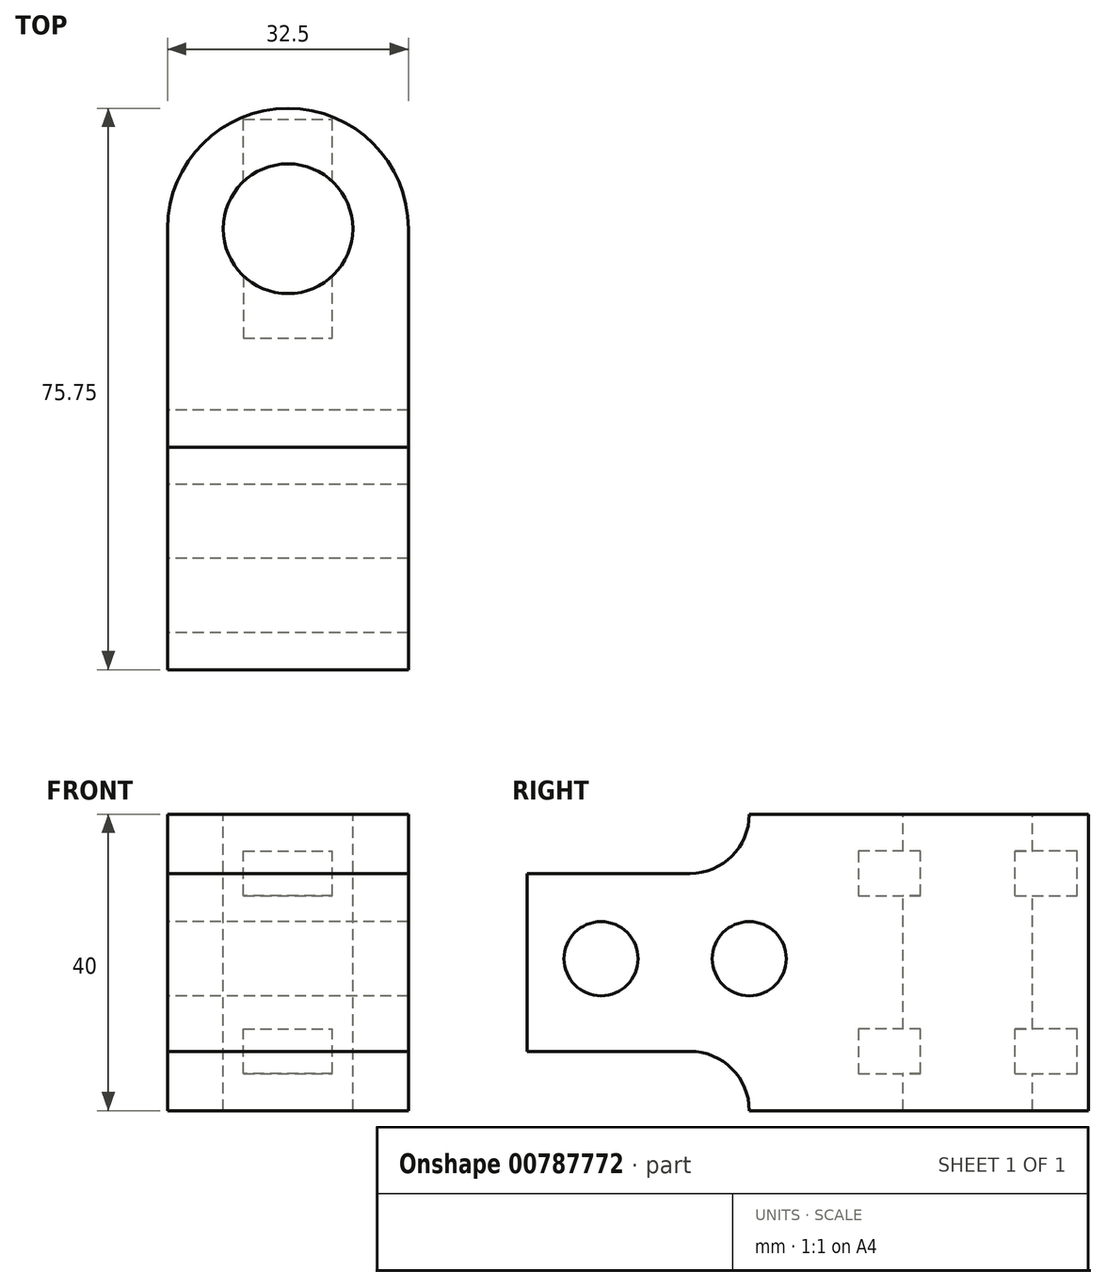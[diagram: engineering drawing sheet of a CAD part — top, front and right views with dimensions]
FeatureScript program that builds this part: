
annotation { "Feature Type Name" : "Feature", "Feature Type Description" : "" }
export const myFeature = defineFeature(function(context is Context, id is Id, definition is map)
    precondition{}
    {
        {
            var Q0;
            Q0=qCreatedBy(makeId("Top.planeOp"),FACE);
            var sketch = newSketch(context, id + "F0", { "sketchPlane" : qUnion([Q0])});
            skLineSegment(sketch, "E0", {"start": v(0, 0) * mm, "end": v(0, -16.25) * mm});
            skLineSegment(sketch, "E1", {"start": v(16.25, 0) * mm, "end": v(16.25, -29.5) * mm});
            skLineSegment(sketch, "E2", {"start": v(-16.25, 0) * mm, "end": v(-16.25, -29.5) * mm});
            skLineSegment(sketch, "E3", {"start": v(-16.25, -29.5) * mm, "end": v(16.25, -29.5) * mm});
            skArc(sketch, "E4", {"start": v(16.25, 0) * mm, "mid": v(0, 16.25) * mm, "end": v(-16.25, 0) * mm});
            skLineSegment(sketch, "E5", {"start": v(-16.25, -29.5) * mm, "end": v(-16.25, -59.5) * mm});
            skLineSegment(sketch, "E6", {"start": v(-16.25, -59.5) * mm, "end": v(16.25, -59.5) * mm});
            skLineSegment(sketch, "E7", {"start": v(16.25, -59.5) * mm, "end": v(16.25, -29.5) * mm});
            skSolve(sketch);
        }
        {
            var Q0;
            Q0=makeQuery(id+"F0.imprint","IMPRINT",FACE,{"disambiguationData":[TD([[makeQuery(id+"F0.imprint","IMPRINT",EDGE,{"derivedFrom":sQuery(id+"F0.wireOp",EDGE,"E1")}),-1.0]])]});
            var Q1;
            Q1=makeQuery(id+"F0.imprint","IMPRINT",FACE,{"disambiguationData":[TD([[makeQuery(id+"F0.imprint","IMPRINT",EDGE,{"derivedFrom":sQuery(id+"F0.wireOp",EDGE,"E3")}),-1.0]])]});
            extrude(context, id + "F1", {"entities" : qUnion([Q0, Q1]), "depth" : 40 * mm, "offsetDistance" : 25 * mm});
        }
        {
            var Q0;
            Q0=makeQuery(id+"F1.opExtrude","SWEPT_FACE",FACE,{"disambiguationData":[OSD([sQuery(id+"F0.wireOp",EDGE,"E2"),sQuery(id+"F0.wireOp",EDGE,"E5")])]});
            var sketch = newSketch(context, id + "F2", { "sketchPlane" : qUnion([Q0])});
            skLineSegment(sketch, "E8", {"start": v(59.5, 0) * mm, "end": v(59.5, 8) * mm});
            skLineSegment(sketch, "E9", {"start": v(59.5, 32) * mm, "end": v(59.5, 40) * mm});
            skLineSegment(sketch, "E10", {"start": v(59.5, 40) * mm, "end": v(29.5, 40) * mm});
            skLineSegment(sketch, "E11", {"start": v(29.5, 40) * mm, "end": v(29.5, 40) * mm});
            skLineSegment(sketch, "E12", {"start": v(37.5, 32) * mm, "end": v(59.5, 32) * mm});
            skPoint(sketch, "E13.visualSharp", {"position": v(29.5, 32) * mm});
            skArc(sketch, "E13.filletArc", {"start": v(29.5, 40) * mm, "mid": v(31.84, 34.34) * mm, "end": v(37.5, 32) * mm});
            skLineSegment(sketch, "E14", {"start": v(29.5, 0) * mm, "end": v(59.5, 0) * mm});
            skLineSegment(sketch, "E15", {"start": v(29.5, 0) * mm, "end": v(29.5, 0) * mm});
            skLineSegment(sketch, "E16", {"start": v(37.5, 8) * mm, "end": v(59.5, 8) * mm});
            skPoint(sketch, "E17.visualSharp", {"position": v(29.5, 8) * mm});
            skArc(sketch, "E17.filletArc", {"start": v(37.5, 8) * mm, "mid": v(31.84, 5.66) * mm, "end": v(29.5, 0) * mm});
            skLineSegment(sketch, "E18", {"start": v(59.5, 8) * mm, "end": v(59.5, 20.5) * mm});
            skCircle(sketch, "E19", {"center": v(29.5, 20.5) * mm, "radius": 5 * mm});
            skCircle(sketch, "E20", {"center": v(49.5, 20.5) * mm, "radius": 5 * mm});
            skSolve(sketch);
        }
        {
            var Q0;
            Q0=makeQuery(id+"F2.imprint","IMPRINT",FACE,{"disambiguationData":[TD([[makeQuery(id+"F2.imprint","IMPRINT",EDGE,{"derivedFrom":sQuery(id+"F2.wireOp",EDGE,"E9")}),-1.0]])]});
            var Q1;
            Q1=makeQuery(id+"F2.imprint","IMPRINT",FACE,{"disambiguationData":[TD([[makeQuery(id+"F2.imprint","IMPRINT",EDGE,{"derivedFrom":sQuery(id+"F2.wireOp",EDGE,"E8")}),-1.0]])]});
            var Q2;
            Q2=makeQuery(id+"F2.imprint","IMPRINT",FACE,{"disambiguationData":[TD([[makeQuery(id+"F2.imprint","IMPRINT",EDGE,{"derivedFrom":sQuery(id+"F2.wireOp",EDGE,"E19")}),1.0]])]});
            var Q3;
            Q3=makeQuery(id+"F2.imprint","IMPRINT",FACE,{"disambiguationData":[TD([[makeQuery(id+"F2.imprint","IMPRINT",EDGE,{"derivedFrom":sQuery(id+"F2.wireOp",EDGE,"E20")}),1.0]])]});
            extrude(context, id + "F3", {"entities" : qUnion([Q0, Q1, Q2, Q3]), "operationType" : NewBodyOperationType.REMOVE, "oppositeDirection" : true, "depth" : 32.5 * mm, "offsetDistance" : 25 * mm});
        }
        {
            var Q0;
            Q0=makeQuery(id+"F1.opExtrude","CAP_FACE",FACE,{"disambiguationData":[OSD([sQuery(id+"F0.wireOp",EDGE,"E1"),sQuery(id+"F0.wireOp",EDGE,"E2"),sQuery(id+"F0.wireOp",EDGE,"E4"),sQuery(id+"F0.wireOp",EDGE,"E5"),sQuery(id+"F0.wireOp",EDGE,"E6"),sQuery(id+"F0.wireOp",EDGE,"E7")])],"isStart":false});
            var sketch = newSketch(context, id + "F4", { "sketchPlane" : qUnion([Q0])});
            skCircle(sketch, "E21", {"center": v(0, 0) * mm, "radius": 8.75 * mm});
            skSolve(sketch);
        }
        {
            var Q0;
            Q0=makeQuery(id+"F4.imprint","IMPRINT",FACE,{"disambiguationData":[TD([[makeQuery(id+"F4.imprint","IMPRINT",EDGE,{"derivedFrom":sQuery(id+"F4.wireOp",EDGE,"E21")}),1.0]])]});
            extrude(context, id + "F5", {"entities" : qUnion([Q0]), "operationType" : NewBodyOperationType.REMOVE, "oppositeDirection" : true, "depth" : 40 * mm, "offsetDistance" : 25 * mm});
        }
        {
            var Q0;
            Q0=qCreatedBy(makeId("Right.planeOp"),FACE);
            var sketch = newSketch(context, id + "F6", { "sketchPlane" : qUnion([Q0])});
            skLineSegment(sketch, "E22", {"start": v(14.75, 5) * mm, "end": v(14.75, 11) * mm});
            skLineSegment(sketch, "E23", {"start": v(14.75, 29) * mm, "end": v(14.75, 35) * mm});
            skLineSegment(sketch, "E24", {"start": v(14.75, 35) * mm, "end": v(0, 35) * mm});
            skLineSegment(sketch, "E25", {"start": v(0, 35) * mm, "end": v(-14.75, 35) * mm});
            skLineSegment(sketch, "E26", {"start": v(-14.75, 35) * mm, "end": v(-14.75, 29) * mm});
            skLineSegment(sketch, "E27", {"start": v(-14.75, 29) * mm, "end": v(14.75, 29) * mm});
            skLineSegment(sketch, "E28", {"start": v(14.75, 11) * mm, "end": v(-14.75, 11) * mm});
            skLineSegment(sketch, "E29", {"start": v(-14.75, 11) * mm, "end": v(-14.75, 5) * mm});
            skLineSegment(sketch, "E30", {"start": v(-14.75, 5) * mm, "end": v(14.75, 5) * mm});
            skSolve(sketch);
        }
        {
            var Q0;
            Q0=makeQuery(id+"F6.imprint","IMPRINT",FACE,{"disambiguationData":[TD([[makeQuery(id+"F6.imprint","IMPRINT",EDGE,{"derivedFrom":sQuery(id+"F6.wireOp",EDGE,"E23")}),1.0]])]});
            var Q1;
            Q1=makeQuery(id+"F6.imprint","IMPRINT",FACE,{"disambiguationData":[TD([[makeQuery(id+"F6.imprint","IMPRINT",EDGE,{"derivedFrom":sQuery(id+"F6.wireOp",EDGE,"E22")}),1.0]])]});
            extrude(context, id + "F7", {"entities" : qUnion([Q0, Q1]), "operationType" : NewBodyOperationType.REMOVE, "endBound" : BoundingType.SYMMETRIC, "oppositeDirection" : true, "depth" : 12 * mm, "offsetDistance" : 25 * mm});
        }
    });
